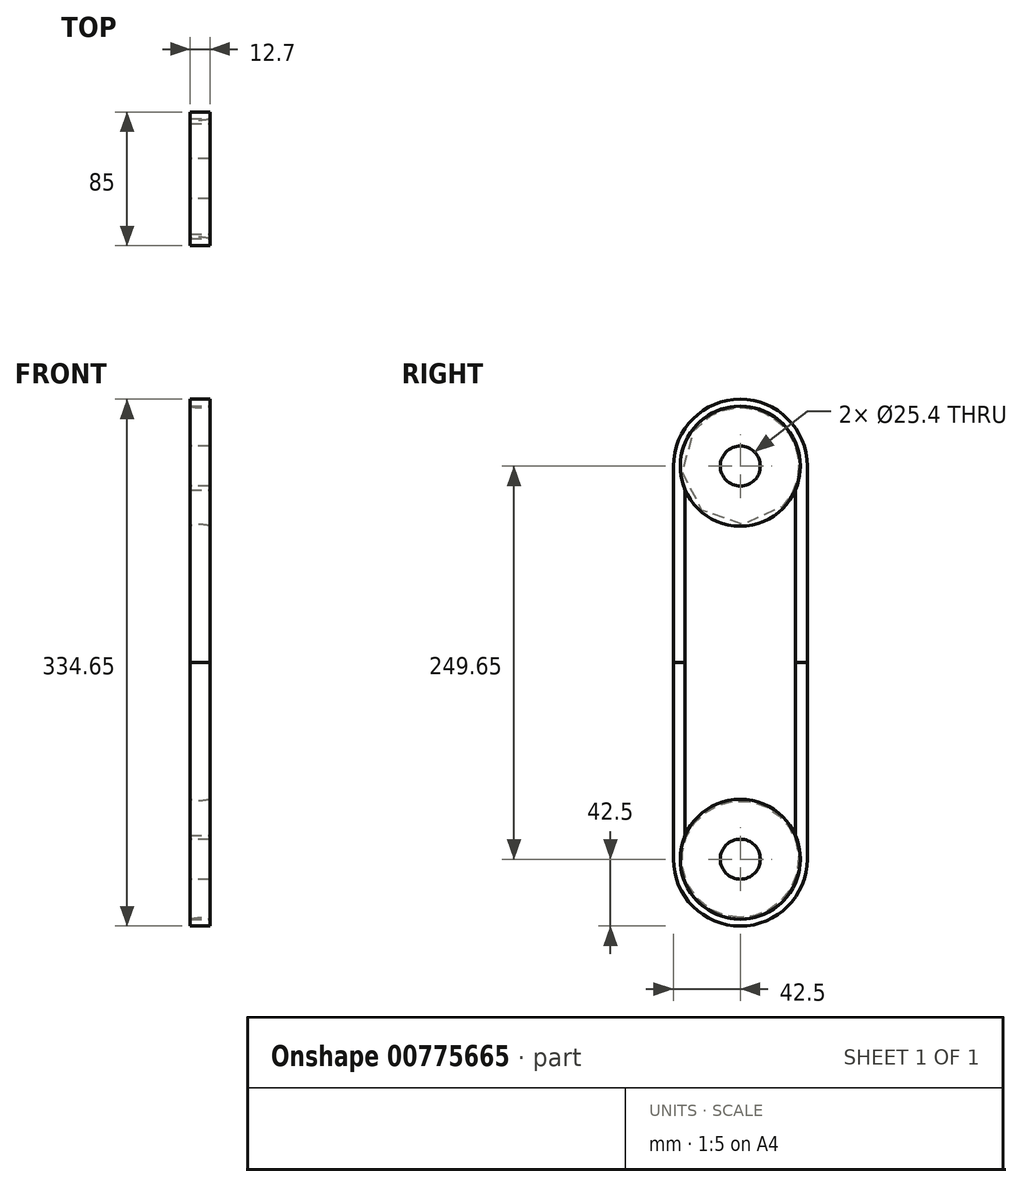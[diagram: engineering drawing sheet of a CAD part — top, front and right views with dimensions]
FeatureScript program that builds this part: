
annotation { "Feature Type Name" : "Feature", "Feature Type Description" : "" }
export const myFeature = defineFeature(function(context is Context, id is Id, definition is map)
    precondition{}
    {
        {
            var Q0;
            Q0=qCreatedBy(makeId("Front.planeOp"),FACE);
            var sketch = newSketch(context, id + "F0", { "sketchPlane" : qUnion([Q0])});
            skLineSegment(sketch, "E0", {"start": v(-10.94, 0) * mm, "end": v(1.76, 0) * mm});
            skLineSegment(sketch, "E1", {"start": v(1.76, 0) * mm, "end": v(1.76, 38.1) * mm});
            skLineSegment(sketch, "E2", {"start": v(1.76, 38.1) * mm, "end": v(-10.94, 38.1) * mm});
            skLineSegment(sketch, "E3", {"start": v(-10.94, 38.1) * mm, "end": v(-10.94, 0) * mm});
            skLineSegment(sketch, "E4", {"start": v(-10.94, 12.7) * mm, "end": v(1.76, 12.7) * mm});
            skArc(sketch, "E5", {"start": v(-10.94, 38.1) * mm, "mid": v(-4.59, 37.08) * mm, "end": v(1.76, 38.1) * mm});
            skSolve(sketch);
        }
        {
            var Q0;
            {var subQ3=sQuery(id+"F0.wireOp",EDGE,"E4");Q0=makeQuery(id+"F0.imprint","IMPRINT",FACE,{"disambiguationData":[TD([[makeQuery(id+"F0.imprint","IMPRINT",EDGE,{"derivedFrom":subQ3}),1.0]])]});}
            var Q1;
            Q1=sQuery(id+"F0.wireOp",EDGE,"E0");
            revolve(context, id + "F1", {"surfaceOperationType" : NewSurfaceOperationType.NEW, "entities" : qUnion([Q0]), "axis" : qUnion([Q1]), "revolveType" : RevolveType.FULL});
        }
        {
            var Q0;
            Q0=qCreatedBy(makeId("Top.planeOp"),FACE);
            cPlane(context, id + "F2", {"entities" : qUnion([Q0]), "cplaneType" : CPlaneType.OFFSET, "offset" : (249.65 / 2) * mm, "oppositeDirection" : true, "width" : 150 * mm, "height" : 150 * mm});
        }
        {
            var Q0;
            Q0=makeQuery(id+"F1.opRevolve","SWEPT_BODY",BODY,{"disambiguationData":[OSD([sQuery(id+"F0.wireOp",EDGE,"E1"),sQuery(id+"F0.wireOp",EDGE,"E3"),sQuery(id+"F0.wireOp",EDGE,"E4"),sQuery(id+"F0.wireOp",EDGE,"E5")])]});
            var Q1;
            Q1=qCreatedBy(id+"F2.planeOp",FACE);
            mirror(context, id + "F3", {"entities" : qUnion([Q0]), "mirrorPlane" : qUnion([Q1])});
        }
        {
            var Q0;
            Q0=makeQuery(id+"F1.opRevolve","SWEPT_FACE",FACE,{"disambiguationData":[OSD([sQuery(id+"F0.wireOp",EDGE,"E1")])]});
            var sketch = newSketch(context, id + "F4", { "sketchPlane" : qUnion([Q0])});
            skCircle(sketch, "E6", {"center": v(0, 0) * mm, "radius": 35 * mm});
            skCircle(sketch, "E7", {"center": v(0, 0) * mm, "radius": 42.5 * mm});
            skLineSegment(sketch, "E8", {"start": v(-42.5, 0) * mm, "end": v(-42.5, -124.83) * mm});
            skLineSegment(sketch, "E9", {"start": v(42.5, 0) * mm, "end": v(42.5, -124.83) * mm});
            skLineSegment(sketch, "E10", {"start": v(35, 0) * mm, "end": v(35, -124.83) * mm});
            skLineSegment(sketch, "E11", {"start": v(35, -124.83) * mm, "end": v(42.5, -124.83) * mm});
            skLineSegment(sketch, "E12", {"start": v(-42.5, -124.83) * mm, "end": v(-35, -124.83) * mm});
            skLineSegment(sketch, "E13", {"start": v(-35, -124.83) * mm, "end": v(-35, 0) * mm});
            skSolve(sketch);
        }
        {
            var Q0;
            {var subQ0=sQuery(id+"F4.wireOp",EDGE,"E8");Q0=makeQuery(id+"F4.imprint","IMPRINT",FACE,{"disambiguationData":[TD([[makeQuery(id+"F4.imprint","IMPRINT",EDGE,{"derivedFrom":subQ0}),1.0]])]});}
            var Q1;
            {var subQ0=sQuery(id+"F4.wireOp",EDGE,"E9");Q1=makeQuery(id+"F4.imprint","IMPRINT",FACE,{"disambiguationData":[TD([[makeQuery(id+"F4.imprint","IMPRINT",EDGE,{"derivedFrom":subQ0}),-1.0]])]});}
            var Q2;
            {var subQ1=sQuery(id+"F4.wireOp",EDGE,"E7");var subQ6=makeQuery(id+"F4.imprint","INTERSECT",VERTEX,{"derivedFrom":[subQ1,sQuery(id+"F4.wireOp",EDGE,"E8")]});Q2=makeQuery(id+"F4.imprint","IMPRINT",FACE,{"disambiguationData":[TD([[makeQuery(id+"F4.imprint","IMPRINT",EDGE,{"disambiguationData":[TD([[subQ6,1.0]])],"derivedFrom":subQ1}),1.0]])]});}
            var Q3;
            Q3=makeQuery(id+"F1.opRevolve","SWEPT_FACE",FACE,{"disambiguationData":[OSD([sQuery(id+"F0.wireOp",EDGE,"E3")])]});
            extrude(context, id + "F5", {"entities" : qUnion([Q0, Q1, Q2]), "endBound" : BoundingType.UP_TO_SURFACE, "oppositeDirection" : true, "depth" : 25 * mm, "endBoundEntityFace" : qUnion([Q3]), "offsetDistance" : 25 * mm});
        }
        {
            var Q0;
            Q0=makeQuery(id+"F5.opExtrude","SWEPT_BODY",BODY,{"disambiguationData":[OSD([sQuery(id+"F0.wireOp",EDGE,"E1"),sQuery(id+"F0.wireOp",EDGE,"E2"),sQuery(id+"F0.wireOp",EDGE,"E5"),sQuery(id+"F4.wireOp",EDGE,"E7"),sQuery(id+"F4.wireOp",EDGE,"E8"),sQuery(id+"F4.wireOp",EDGE,"E9"),sQuery(id+"F4.wireOp",EDGE,"E10"),sQuery(id+"F4.wireOp",EDGE,"E11"),sQuery(id+"F4.wireOp",EDGE,"E12"),sQuery(id+"F4.wireOp",EDGE,"E13")])]});
            var Q1;
            Q1=qCreatedBy(id+"F2.planeOp",FACE);
            mirror(context, id + "F6", {"operationType" : NewBodyOperationType.ADD, "entities" : qUnion([Q0]), "mirrorPlane" : qUnion([Q1])});
        }
    });
